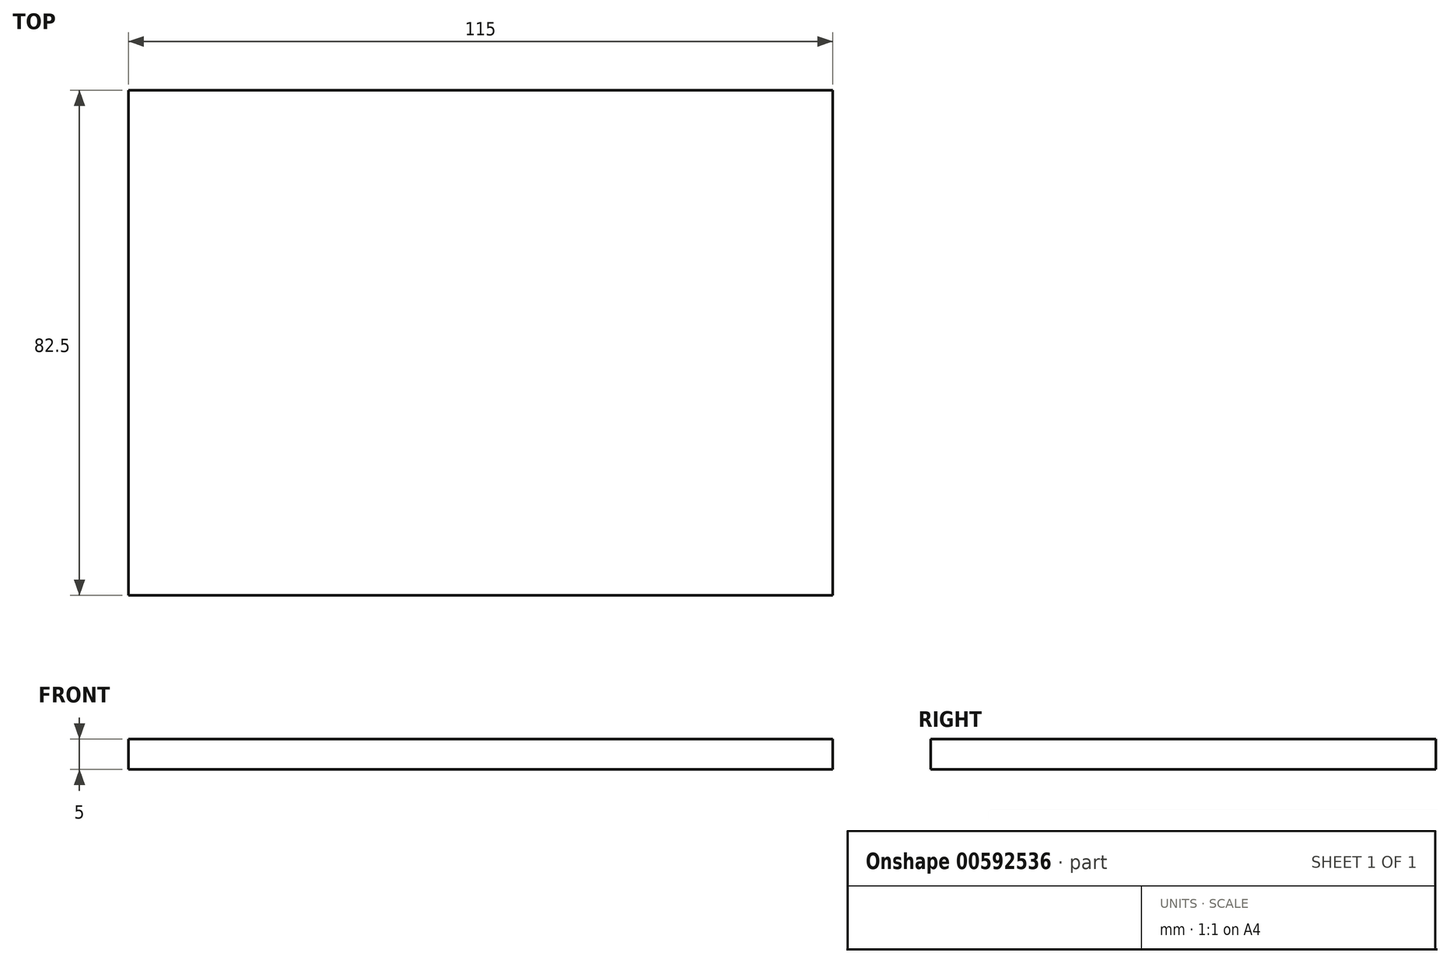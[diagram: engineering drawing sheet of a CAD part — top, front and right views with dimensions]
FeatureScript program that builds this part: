
annotation { "Feature Type Name" : "Feature", "Feature Type Description" : "" }
export const myFeature = defineFeature(function(context is Context, id is Id, definition is map)
    precondition{}
    {
        {
            var Q0;
            Q0=qCreatedBy(makeId("Top.planeOp"),FACE);
            var sketch = newSketch(context, id + "F0", { "sketchPlane" : qUnion([Q0])});
            skLineSegment(sketch, "E0.bottom", {"start": v(-57.5, 41.25) * mm, "end": v(57.5, 41.25) * mm});
            skLineSegment(sketch, "E0.top", {"start": v(-57.5, -41.25) * mm, "end": v(57.5, -41.25) * mm});
            skLineSegment(sketch, "E0.left", {"start": v(-57.5, 41.25) * mm, "end": v(-57.5, -41.25) * mm});
            skLineSegment(sketch, "E0.right", {"start": v(57.5, 41.25) * mm, "end": v(57.5, -41.25) * mm});
            skSolve(sketch);
        }
        {
            var Q0;
            Q0=makeQuery(id+"F0.imprint","IMPRINT",FACE,{"disambiguationData":[TD([[makeQuery(id+"F0.imprint","IMPRINT",EDGE,{"derivedFrom":sQuery(id+"F0.wireOp",EDGE,"E0.bottom")}),-1.0]])]});
            extrude(context, id + "F1", {"entities" : qUnion([Q0]), "depth" : 5 * mm, "offsetDistance" : 25 * mm});
        }
    });
